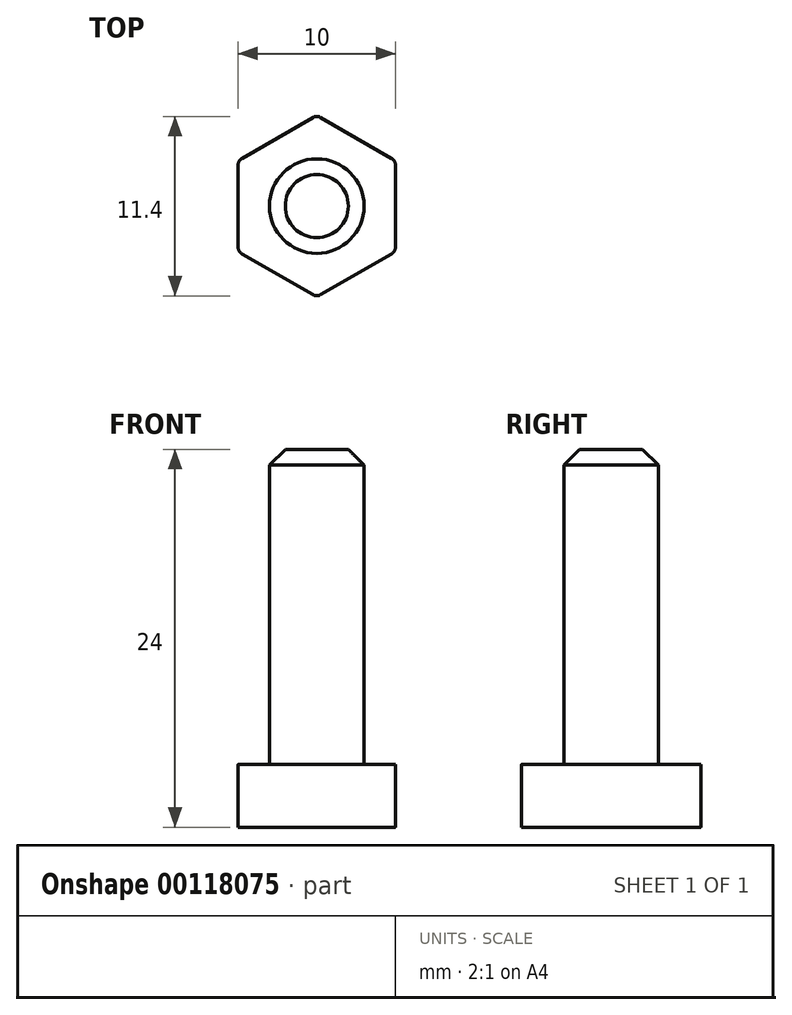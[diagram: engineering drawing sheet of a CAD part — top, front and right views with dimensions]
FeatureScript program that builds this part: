
annotation { "Feature Type Name" : "Feature", "Feature Type Description" : "" }
export const myFeature = defineFeature(function(context is Context, id is Id, definition is map)
    precondition{}
    {
        {
            var Q0;
            Q0=qCreatedBy(makeId("Top.planeOp"),FACE);
            var sketch = newSketch(context, id + "F0", { "sketchPlane" : qUnion([Q0])});
            skCircle(sketch, "E0.cCircle", {"center": v(0, 0) * mm, "radius": 5 * mm, "construction": true});
            skLineSegment(sketch, "E0.0", {"start": v(5, 2.89) * mm, "end": v(5, -2.89) * mm});
            skLineSegment(sketch, "E0.1", {"start": v(5, -2.89) * mm, "end": v(0, -5.77) * mm});
            skLineSegment(sketch, "E0.2", {"start": v(0, -5.77) * mm, "end": v(-5, -2.89) * mm});
            skLineSegment(sketch, "E0.3", {"start": v(-5, -2.89) * mm, "end": v(-5, 2.89) * mm});
            skLineSegment(sketch, "E0.4", {"start": v(-5, 2.89) * mm, "end": v(0, 5.77) * mm});
            skLineSegment(sketch, "E0.5", {"start": v(0, 5.77) * mm, "end": v(5, 2.89) * mm});
            skPoint(sketch, "E0.0.midPoint", {"position": v(5, 0) * mm});
            skSolve(sketch);
        }
        {
            var Q0;
            Q0=makeQuery(id+"F0.imprint","IMPRINT",FACE,{"disambiguationData":[TD([[makeQuery(id+"F0.imprint","IMPRINT",EDGE,{"derivedFrom":sQuery(id+"F0.wireOp",EDGE,"E0.0")}),-1.0]])]});
            extrude(context, id + "F1", {"entities" : qUnion([Q0]), "depth" : 4 * mm});
        }
        {
            var Q0;
            Q0=makeQuery(id+"F1.opExtrude","CAP_FACE",FACE,{"disambiguationData":[OSD([sQuery(id+"F0.wireOp",EDGE,"E0.0"),sQuery(id+"F0.wireOp",EDGE,"E0.1"),sQuery(id+"F0.wireOp",EDGE,"E0.2"),sQuery(id+"F0.wireOp",EDGE,"E0.3"),sQuery(id+"F0.wireOp",EDGE,"E0.4"),sQuery(id+"F0.wireOp",EDGE,"E0.5")])],"isStart":false});
            var sketch = newSketch(context, id + "F2", { "sketchPlane" : qUnion([Q0])});
            skCircle(sketch, "E1", {"center": v(0, 0) * mm, "radius": 3 * mm});
            skSolve(sketch);
        }
        {
            var Q0;
            Q0=makeQuery(id+"F2.imprint","IMPRINT",FACE,{"disambiguationData":[TD([[makeQuery(id+"F2.imprint","IMPRINT",EDGE,{"derivedFrom":sQuery(id+"F2.wireOp",EDGE,"E1")}),1.0]])]});
            extrude(context, id + "F3", {"entities" : qUnion([Q0]), "operationType" : NewBodyOperationType.ADD, "depth" : 20 * mm});
        }
        {
            var Q0;
            Q0=makeQuery(id+"F3.opExtrude","CAP_EDGE",EDGE,{"disambiguationData":[OSD([sQuery(id+"F2.wireOp",EDGE,"E1")])],"isStart":false});
            chamfer(context, id + "F4", {"entities" : qUnion([Q0]), "width" : 1 * mm, "tangentPropagation" : true});
        }
        {
            var Q0;
            Q0=makeQuery(id+"F1.opExtrude","SWEPT_EDGE",EDGE,{"disambiguationData":[OSD([sQuery(id+"F0.wireOp",EDGE,"E0.1"),sQuery(id+"F0.wireOp",EDGE,"E0.2")])]});
            var Q1;
            Q1=makeQuery(id+"F1.opExtrude","SWEPT_EDGE",EDGE,{"disambiguationData":[OSD([sQuery(id+"F0.wireOp",EDGE,"E0.0"),sQuery(id+"F0.wireOp",EDGE,"E0.1")])]});
            var Q2;
            Q2=makeQuery(id+"F1.opExtrude","SWEPT_EDGE",EDGE,{"disambiguationData":[OSD([sQuery(id+"F0.wireOp",EDGE,"E0.0"),sQuery(id+"F0.wireOp",EDGE,"E0.5")])]});
            var Q3;
            Q3=makeQuery(id+"F1.opExtrude","SWEPT_EDGE",EDGE,{"disambiguationData":[OSD([sQuery(id+"F0.wireOp",EDGE,"E0.2"),sQuery(id+"F0.wireOp",EDGE,"E0.3")])]});
            var Q4;
            Q4=makeQuery(id+"F1.opExtrude","SWEPT_EDGE",EDGE,{"disambiguationData":[OSD([sQuery(id+"F0.wireOp",EDGE,"E0.4"),sQuery(id+"F0.wireOp",EDGE,"E0.5")])]});
            var Q5;
            Q5=makeQuery(id+"F1.opExtrude","SWEPT_EDGE",EDGE,{"disambiguationData":[OSD([sQuery(id+"F0.wireOp",EDGE,"E0.3"),sQuery(id+"F0.wireOp",EDGE,"E0.4")])]});
            fillet(context, id + "F5", {"entities" : qUnion([Q0, Q1, Q2, Q3, Q4, Q5]), "radius" : .5 * mm, "tangentPropagation" : true, "allowEdgeOverflow" : false});
        }
    });
